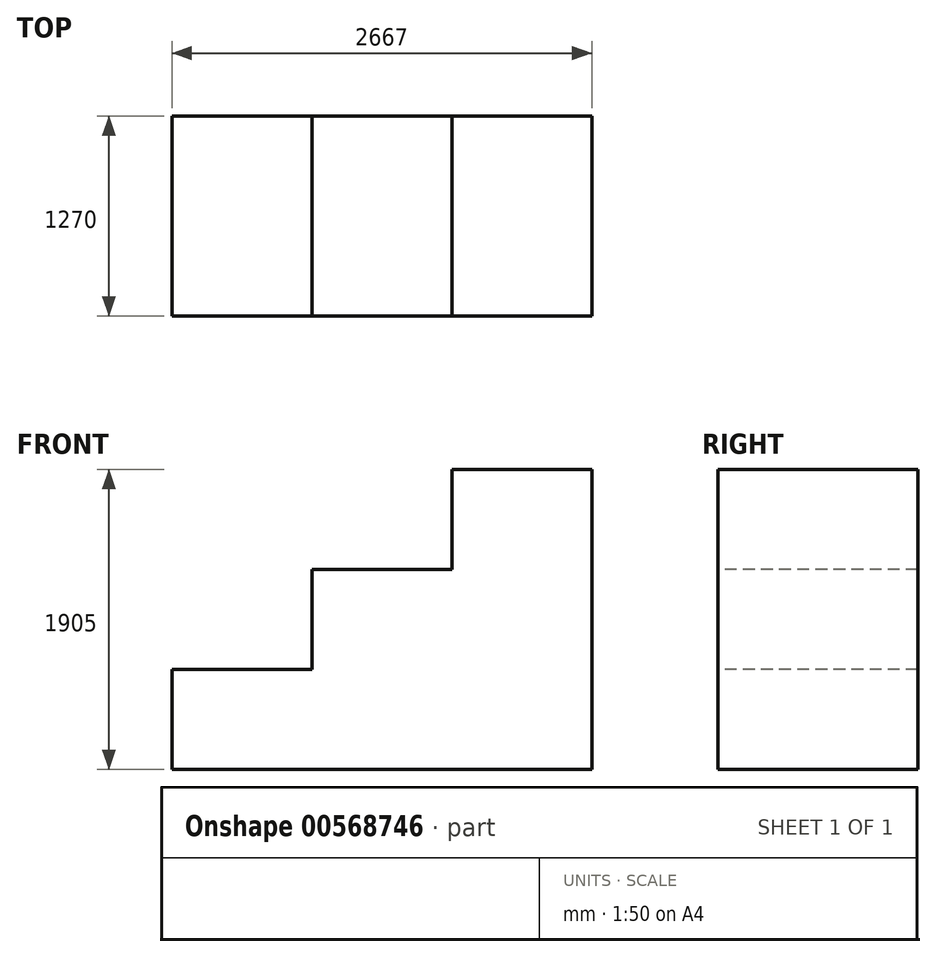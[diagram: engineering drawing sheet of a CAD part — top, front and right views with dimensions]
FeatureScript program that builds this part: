
annotation { "Feature Type Name" : "Feature", "Feature Type Description" : "" }
export const myFeature = defineFeature(function(context is Context, id is Id, definition is map)
    precondition{}
    {
        {
            var Q0;
            Q0=qCreatedBy(makeId("Front.planeOp"),FACE);
            var sketch = newSketch(context, id + "F0", { "sketchPlane" : qUnion([Q0])});
            skLineSegment(sketch, "E0.bottom", {"start": v(2536.52, 1836.71) * mm, "end": v(-130.48, 1836.71) * mm});
            skLineSegment(sketch, "E0.top", {"start": v(2536.52, -68.29) * mm, "end": v(-130.48, -68.29) * mm});
            skLineSegment(sketch, "E0.left", {"start": v(2536.52, 1836.71) * mm, "end": v(2536.52, -68.29) * mm});
            skLineSegment(sketch, "E0.right", {"start": v(-130.48, 1836.71) * mm, "end": v(-130.48, -68.29) * mm});
            skSolve(sketch);
        }
        {
            var Q0;
            Q0 = qSketchRegion(id + "F0", true);
            extrude(context, id + "F1", {"entities" : qUnion([Q0]), "oppositeDirection" : true, "depth" : 1270 * mm, "offsetDistance" : 25.4 * mm});
        }
        {
            var Q0;
            Q0=makeQuery(id+"F1.opExtrude","CAP_FACE",FACE,{"disambiguationData":[OSD([sQuery(id+"F0.wireOp",EDGE,"E0.bottom"),sQuery(id+"F0.wireOp",EDGE,"E0.top"),sQuery(id+"F0.wireOp",EDGE,"E0.left"),sQuery(id+"F0.wireOp",EDGE,"E0.right")])],"isStart":true});
            var sketch = newSketch(context, id + "F2", { "sketchPlane" : qUnion([Q0])});
            skLineSegment(sketch, "E1.bottom", {"start": v(-130.48, 1836.71) * mm, "end": v(758.52, 1836.71) * mm});
            skLineSegment(sketch, "E1.top", {"start": v(-130.48, 566.71) * mm, "end": v(758.52, 566.71) * mm});
            skLineSegment(sketch, "E1.left", {"start": v(-130.48, 1836.71) * mm, "end": v(-130.48, 566.71) * mm});
            skLineSegment(sketch, "E1.right", {"start": v(758.52, 1836.71) * mm, "end": v(758.52, 566.71) * mm});
            skSolve(sketch);
        }
        {
            var Q0;
            Q0 = qSketchRegion(id + "F2", true);
            extrude(context, id + "F3", {"entities" : qUnion([Q0]), "operationType" : NewBodyOperationType.REMOVE, "endBound" : BoundingType.THROUGH_ALL, "oppositeDirection" : true, "depth" : 25.4 * mm, "offsetDistance" : 25.4 * mm});
        }
        {
            var Q0;
            Q0=makeQuery(id+"F1.opExtrude","CAP_FACE",FACE,{"disambiguationData":[OSD([sQuery(id+"F0.wireOp",EDGE,"E0.bottom"),sQuery(id+"F0.wireOp",EDGE,"E0.top"),sQuery(id+"F0.wireOp",EDGE,"E0.left"),sQuery(id+"F0.wireOp",EDGE,"E0.right")])],"isStart":true});
            var sketch = newSketch(context, id + "F4", { "sketchPlane" : qUnion([Q0])});
            skLineSegment(sketch, "E2.bottom", {"start": v(758.52, 1836.71) * mm, "end": v(1647.52, 1836.71) * mm});
            skLineSegment(sketch, "E2.top", {"start": v(758.52, 1201.71) * mm, "end": v(1647.52, 1201.71) * mm});
            skLineSegment(sketch, "E2.left", {"start": v(758.52, 1836.71) * mm, "end": v(758.52, 1201.71) * mm});
            skLineSegment(sketch, "E2.right", {"start": v(1647.52, 1836.71) * mm, "end": v(1647.52, 1201.71) * mm});
            skSolve(sketch);
        }
        {
            var Q0;
            Q0 = qSketchRegion(id + "F4", true);
            extrude(context, id + "F5", {"entities" : qUnion([Q0]), "operationType" : NewBodyOperationType.REMOVE, "endBound" : BoundingType.THROUGH_ALL, "oppositeDirection" : true, "depth" : 25.4 * mm, "offsetDistance" : 25.4 * mm});
        }
    });
